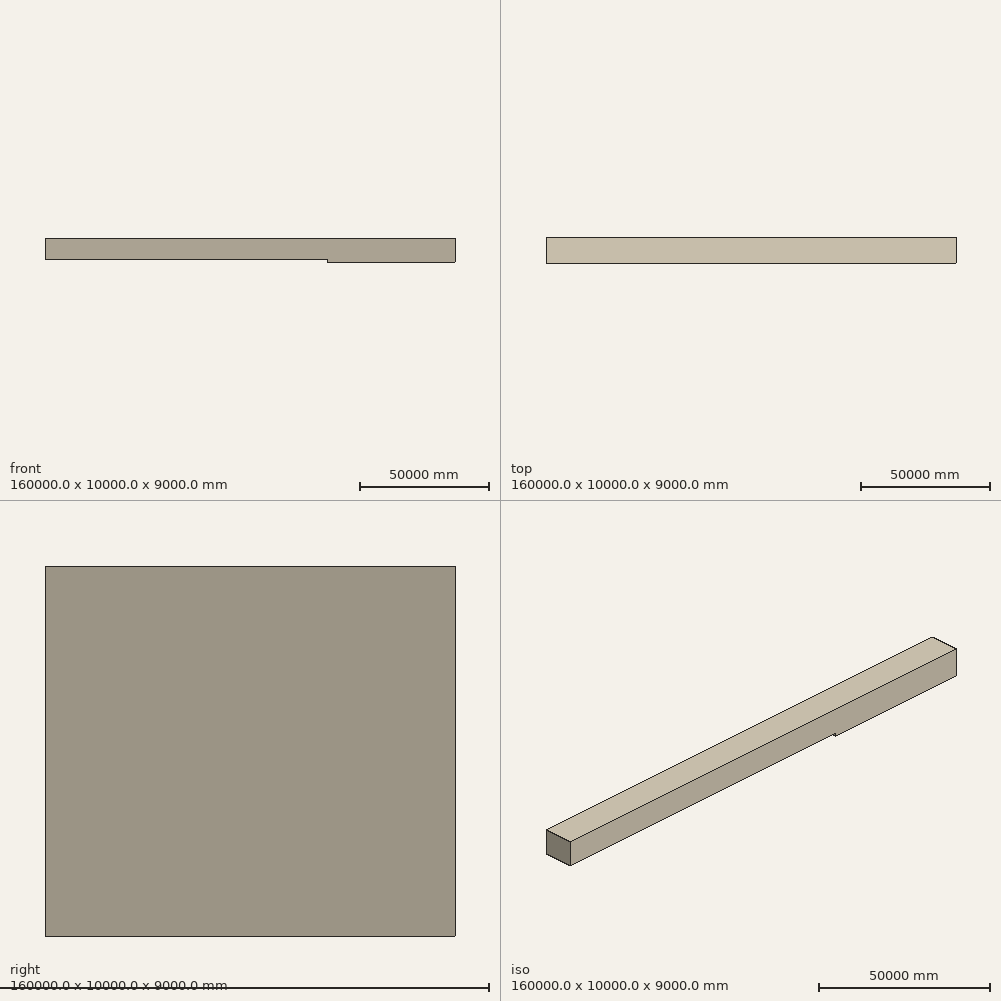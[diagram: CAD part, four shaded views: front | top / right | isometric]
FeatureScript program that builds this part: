
annotation { "Feature Type Name" : "Feature", "Feature Type Description" : "" }
export const myFeature = defineFeature(function(context is Context, id is Id, definition is map)
    precondition{}
    {
        {
            var Q0;
            Q0=qCreatedBy(makeId("Front.planeOp"),FACE);
            var sketch = newSketch(context, id + "F0", { "sketchPlane" : qUnion([Q0])});
            skLineSegment(sketch, "E0", {"start": v(8713.42, -8000) * mm, "end": v(118713.42, -8000) * mm});
            skLineSegment(sketch, "E1", {"start": v(118713.42, -8000) * mm, "end": v(118713.42, -9000) * mm});
            skLineSegment(sketch, "E2", {"start": v(118713.42, -9000) * mm, "end": v(168713.42, -9000) * mm});
            skLineSegment(sketch, "E3", {"start": v(168713.42, 0) * mm, "end": v(168713.42, -9000) * mm});
            skLineSegment(sketch, "E4", {"start": v(168713.42, 0) * mm, "end": v(8713.42, 0) * mm});
            skLineSegment(sketch, "E5", {"start": v(8713.42, 0) * mm, "end": v(8713.42, -8000) * mm});
            skSolve(sketch);
        }
        {
            var Q0;
            Q0=makeQuery(id+"F0.imprint","IMPRINT",FACE,{"disambiguationData":[TD([[makeQuery(id+"F0.imprint","IMPRINT",EDGE,{"derivedFrom":sQuery(id+"F0.wireOp",EDGE,"E0")}),1.0]])]});
            extrude(context, id + "F1", {"entities" : qUnion([Q0]), "depth" : 10000 * mm});
        }
        {
            var Q0;
            Q0=makeQuery(id+"F1.opExtrude","SWEPT_BODY",BODY,{"disambiguationData":[OSD([sQuery(id+"F0.wireOp",EDGE,"E0"),sQuery(id+"F0.wireOp",EDGE,"E1"),sQuery(id+"F0.wireOp",EDGE,"E2"),sQuery(id+"F0.wireOp",EDGE,"E3"),sQuery(id+"F0.wireOp",EDGE,"E4"),sQuery(id+"F0.wireOp",EDGE,"Q1THugad-maSY-Kkpk-r2RX-xoeFdePFvmjI"),sQuery(id+"F0.wireOp",EDGE,"ZXpMDo6r-4JGg-3uCC-UvOq-HwgmJIDT5aIP"),sQuery(id+"F0.wireOp",EDGE,"5UwzPdSp-7CAN-CLka-K1wM-Kq5EZqgptbQ7")])]});
            transform(context, id + "F2", {"entities" : qUnion([Q0]), "transformType" : TransformType.TRANSLATION_3D, "dx" : -118710 * mm, "dy" : 5000 * mm, "dz" : 9000 * mm, "makeCopy" : false});
        }
    });
